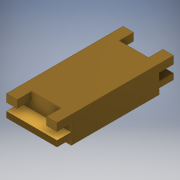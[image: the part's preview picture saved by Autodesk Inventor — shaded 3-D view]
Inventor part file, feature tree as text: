
AUTODESK INVENTOR PART (.ipt)
format: ipt  version: 2019.4 (Build 234330000, 330)  size: 168,960 bytes
history: native  units: in
note: dims shown in document units (in); Inventor stores cm internally (conversion verified against a paired STEP export)
features: extrude x4, sketch x4
ambient origin geometry x8: Origin, YZ Plane, XZ Plane, XY Plane, X Axis, Y Axis, Z Axis, Center Point
bodies: Solid1 (feature_tree)
feature tree (8):
  extrude  "Extrusion1"  Depth=1.0354in
  extrude  "Extrusion2"  Depth=0.2953in
  extrude  "Extrusion3"  Depth=0.1575in TaperAngle=0.0deg
  extrude  "Extrusion4"  Depth=0.1181in
  sketch  "Sketch1"  dims[d0=1.7992in d1=1.0354in]
  sketch  "Sketch2"  dims[d2=0.5512in d3=0.0in d4=0.2953in]
  sketch  "Sketch3"  dims[d5=0.2165in d6=0.1575in d7=0.0in]
  sketch  "Sketch4"  dims[d8=0.1575in d9=0.1181in d10=0.1575in d11=0.1181in d12=1.0354in d13=0.0in d14=0.1969in d15=0.4331in d16=0.1969in d17=0.4331in d18=0.0787in d19=0.0in]
